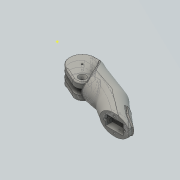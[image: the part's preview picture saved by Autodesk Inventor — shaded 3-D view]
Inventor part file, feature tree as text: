
AUTODESK INVENTOR PART (.ipt)
format: ipt  version: 2016 (Build 200138000, 138)  size: 2,577,408 bytes
history: native  units: mm
features: sketch x48, plane x35, extrude x21, fillet x17, chamfer x4, other x3, sweep x2, projected_geometry x2, loft x1, mirror x1, thicken_offset x1
ambient origin geometry x8: Origin, YZ Plane, XZ Plane, XY Plane, X Axis, Y Axis, Z Axis, Center Point
bodies: Body1 (feature_tree)
feature tree (135):
  sketch  "Sketch1"  dims[d1=8.0mm d2=7.0mm]
  plane  "Work Plane4"
  sketch  "Sketch2"  dims[d3=7.0mm d4=8.0mm d8=20.0mm d9=-3.490659mm d11=8.0mm d12=8.0mm d14=2.0mm d15=10.0mm d17=-1.745329mm d18=1.0mm d19=11.75mm]
  sketch  "Sketch3"  dims[d20=20.0mm d21=9.5mm]
  sketch  "Sketch4"  dims[d22=8.0mm d23=0.0mm d25=9.0mm]
  sketch  "Sketch5"  dims[d27=8.5mm d28=3.0mm]
  sketch  "Sketch6"  dims[d29=-1.745329mm d30=-3.490659mm d31=1.0mm d32=2.0mm d33=8.6mm]
  plane  "Work Plane5"
  sketch  "Sketch7"  dims[d34=8.5mm d35=7.0mm]
  plane  "Work Plane7"
  sketch  "Sketch8"  dims[d36=7.0mm d37=5.0mm d38=3.0mm]
  plane  "Work Plane8"
  sketch  "Sketch9"  dims[d39=17.0mm]
  plane  "Work Plane10"
  sketch  "Sketch10"  dims[d40=8.0mm]
  plane  "Work Plane11"
  plane  "Work Plane12"
  sketch  "Sketch11"  dims[d41=17.0mm]
  sketch  "Sketch12"  dims[d42=7.7mm]
  sketch  "Sketch13"  dims[d43=17.0mm]
  plane  "Work Plane13"
  plane  "Work Plane14"
  plane  "Work Plane15"
  plane  "Work Plane16"
  sketch  "Sketch14"  dims[d44=6.8mm]
  sketch  "Sketch15"  dims[d45=17.0mm]
  plane  "Work Plane20"
  sketch  "Sketch16"  dims[d46=5.0mm]
  sketch  "Sketch17"  dims[d47=2.0mm]
  sketch  "Sketch18"  dims[d48=17.0mm]
  sketch  "Sketch19"  dims[d49=2.0mm]
  plane  "Work Plane21"
  loft  "Loft1"
  extrude  "Extrusion1"  Depth=20.0mm
  fillet  "Fillet1"  [1 undecoded]
  fillet  "Fillet2"  Radius=8.0mm
  fillet  "Fillet3"  Radius=2.0mm
  fillet  "Fillet4"  Radius=10.0mm
  fillet  "Fillet5"  Radius=1.0mm
  fillet  "Fillet6"  Radius=11.75mm
  plane  "Work Plane23"
  plane  "Work Plane25"
  sketch  "Sketch22"  dims[d75=0.0mm d76=90.0deg d77=0.0mm d78=90.0deg d79=0.0mm d80=90.0deg]
  extrude  "Extrusion2"  Depth=9.5mm
  plane  "Work Plane26"
  sketch  "Sketch24"  dims[d85=0.3mm d86=6.0mm]
  sketch  "Sketch25"  dims[d87=6.0mm d88=2.0mm]
  extrude  "Extrusion3"  Depth=9.0mm
  extrude  "Extrusion4"  Depth=3.0mm
  sketch  "Sketch27"  dims[d90=2.0mm]
  extrude  "Extrusion5"  Depth=8.6mm
  sketch  "Sketch29"  dims[d96=2.0mm d97=2.0mm]
  extrude  "Extrusion6"  Depth=7.0mm
  extrude  "Extrusion7"  Depth=5.0mm
  mirror  "Mirror1"
  chamfer  "Chamfer1"  Angle=90.0deg  [1 undecoded]
  fillet  "Fillet7"  [1 undecoded]
  fillet  "Fillet8"  [1 undecoded]
  fillet  "Fillet9"  [1 undecoded]
  fillet  "Fillet10"  [1 undecoded]
  chamfer  "Chamfer2"  Angle=90.0deg  [1 undecoded]
  fillet  "Fillet12"  [1 undecoded]
  fillet  "Fillet13"  [1 undecoded]
  fillet  "Fillet14"  [1 undecoded]
  fillet  "Fillet17"  [1 undecoded]
  sketch  "Sketch31"  dims[d100=90.0deg d101=22.0mm d102=12.217305mm d103=20.0mm d110=3.0mm]
  plane  "Work Plane27"
  extrude  "Extrusion9"  TaperAngle=0.0deg  [1 undecoded]
  extrude  "Extrusion10"  TaperAngle=0.0deg  [1 undecoded]
  chamfer  "Chamfer4"  Angle=90.0deg  [1 undecoded]
  extrude  "Extrusion11"  TaperAngle=0.0deg  [1 undecoded]
  extrude  "Extrusion12"  Depth=6.0mm
  extrude  "Extrusion13"  Depth=2.0mm
  chamfer  "Chamfer5"  Distance=15.0mm
  plane  "Work Plane28"
  fillet  "Fillet19"  Radius=2.0mm
  fillet  "Fillet20"  Radius=2.0mm
  plane  "Work Plane37"
  extrude  "Extrusion25"  Depth=2.0mm
  extrude  "Extrusion27"  Depth=2.0mm
  extrude  "Extrusion28"  Depth=12.217305mm
  plane  "Work Plane38"
  fillet  "Fillet21"  Radius=3.0mm
  plane  "Work Plane39"
  plane  "Work Plane40"
  plane  "Work Plane42"
  extrude  "Extrusion35"  Depth=8.0mm
  plane  "Work Plane44"
  sweep  "Sweep9"
  sketch  "Sketch80"  dims[d142=8.0mm]
  thicken_offset  "Thicken2"
  extrude  "Extrusion38"  Depth=20.0mm
  extrude  "Extrusion39"  Depth=2.0mm
  other  "Work Axis2"
  other  "Work Point7"
  other  "Work Point8"
  extrude  "Extrusion32"  Depth=4.0mm
  extrude  "Extrusion33"  Depth=6.0mm
  sketch  "Sketch71"  dims[d136=2.0mm]
  sketch  "Sketch72"  dims[d137=12.0mm]
  sweep  "Sweep8"
  sketch  "Sketch74"  dims[d138=6.0mm d139=0.0mm]
  plane  "Work Plane43"
  extrude  "Extrusion36"  Depth=9.0mm
  plane  "Work Plane1"
  plane  "Work Plane2"
  plane  "Work Plane3"
  plane  "Work Plane6"
  plane  "Work Plane9"
  plane  "Work Plane17"
  plane  "Work Plane18"
  plane  "Work Plane19"
  sketch  "Sketch20"  dims[d50=2.0mm d51=0.0mm d52=90.0deg d53=0.0mm d54=90.0deg d55=0.0mm d56=90.0deg d57=0.0mm d58=90.0deg d59=0.0mm d60=90.0deg d61=0.0mm d62=90.0deg d63=0.0mm d64=90.0deg d65=0.0mm d66=90.0deg d67=0.0mm d68=90.0deg d69=0.0mm d70=90.0deg]
  sketch  "Sketch21"  dims[d71=0.0mm d72=90.0deg d73=0.0mm d74=90.0deg]
  plane  "Work Plane22"
  plane  "Work Plane24"
  sketch  "Sketch23"  dims[d81=0.0mm d82=90.0deg d83=0.0mm d84=90.0deg]
  sketch  "Sketch26"  dims[d89=135.0deg]
  sketch  "Sketch28"  dims[d91=45.0deg d92=15.0mm d93=0.0mm d94=2.0mm d95=2.0mm]
  sketch  "Sketch30"  dims[d98=2.0mm d99=2.0mm]
  sketch  "Sketch32"  dims[d111=6.0mm d112=8.0mm]
  sketch  "Sketch33"  dims[d113=6.0mm d114=20.0mm d115=0.0mm]
  sketch  "Sketch34"  dims[d116=12.0mm d117=20.0mm]
  sketch  "Sketch35"  dims[d118=10.0mm d123=2.0mm]
  sketch  "Sketch36"  dims[d124=4.0mm d125=4.0mm]
  sketch  "Sketch58"  dims[d126=12.0mm d127=6.0mm]
  sketch  "Sketch59"  dims[d128=6.0mm d129=0.0mm d130=10.75mm]
  sketch  "Sketch60"  dims[d131=9.0mm d132=9.0mm]
  sketch  "Sketch68"  dims[d133=60.0mm d134=0.0mm]
  sketch  "Sketch70"  dims[d135=30.0mm]
  projected_geometry  "Projected Loop1"
  sketch  "Sketch76"  dims[d140=1.2mm]
  sketch  "Sketch77"  dims[d141=8.0mm]
  projected_geometry  "Projected Loop2"
  sketch  "Sketch81"  dims[d143=1.2mm d144=12.0mm d145=0.0mm d146=20.0mm d147=0.0mm d148=0.5mm d149=2.0mm d150=45.0deg d151=1.0mm d152=0.5mm d153=0.5mm d154=1.0mm d156=0.5mm d157=2.0mm d158=45.0deg d159=1.0mm d160=0.5mm d161=1.0mm d164=0.5mm d167=4.2mm d168=0.0mm d172=4.5mm d173=2.7mm d174=0.0mm d175=2.0mm d176=2.0mm d177=45.0deg d178=2.8mm d179=0.0mm d180=14.0mm d181=4.2mm d182=0.0mm d183=2.8mm d184=0.0mm d185=2.0mm d186=2.0mm d187=45.0deg d188=60.0deg d262=3.85mm d263=1.0mm d264=0.25mm d265=-31.0mm d272=72.0mm d273=24.0mm d274=16.0mm d275=10.0mm d276=0.0mm d277=72.5mm d278=12.7mm d279=7.5mm d280=0.5mm d281=2.0mm d282=0.5mm d283=2.0mm d284=72.5mm d286=1.5mm d287=1.0mm d288=1.5mm d289=1.0mm d292=4.0mm d293=0.0mm d294=2.0mm d295=0.5mm d296=2.0mm d297=0.0mm d313=0.25mm d315=-2.1mm d316=52.0mm d317=10.2mm d318=7.5mm d321=2.0mm d322=0.5mm d323=0.5mm d324=2.0mm d325=1.0mm d326=1.5mm d327=1.0mm d328=1.5mm d329=4.0mm d330=0.0mm d335=2.0mm d337=2.0mm d338=0.0mm d339=57.6mm d340=3.0mm d341=3.0mm d342=2.0mm d362=0.0mm d363=0.0mm d368=4.5mm d369=1.5mm d370=0.0mm d371=2.0mm d374=1.5mm d375=0.0mm d376=23.343mm d380=2.1mm d381=0.15mm d382=0.0mm d383=0.0mm d384=1.0mm d385=1.0mm d386=1.0mm d387=0.0mm d388=12.0mm d389=0.0mm]
note: 15 required parameter values undecoded (feature->parameter linkage not recoverable at this tier; creation-order binding heuristic only, values carry confidence <= 0.55)
